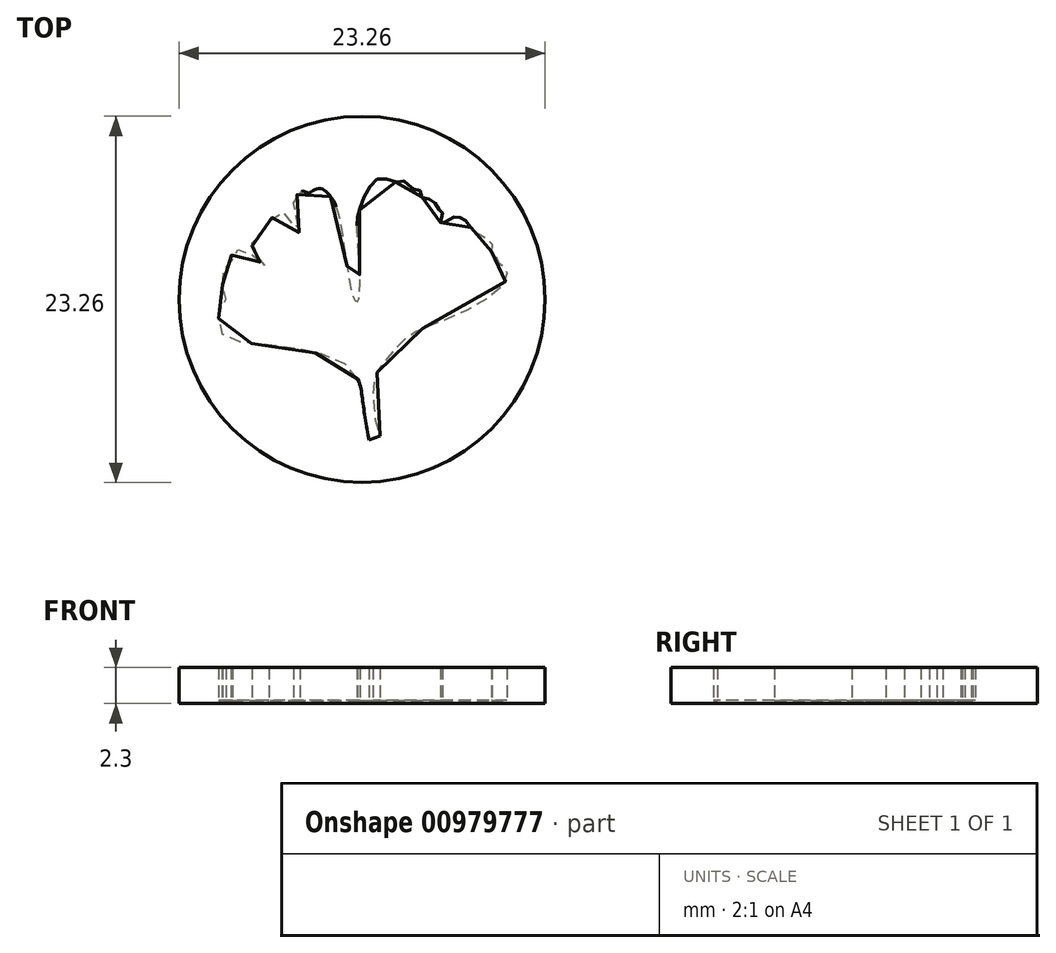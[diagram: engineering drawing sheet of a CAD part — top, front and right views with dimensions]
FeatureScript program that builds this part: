
annotation { "Feature Type Name" : "Feature", "Feature Type Description" : "" }
export const myFeature = defineFeature(function(context is Context, id is Id, definition is map)
    precondition{}
    {
        {
            var Q0;
            Q0=qCreatedBy(makeId("Top.planeOp"),FACE);
            var sketch = newSketch(context, id + "F0", { "sketchPlane" : qUnion([Q0]), "disableImprinting" : false});
            skCircle(sketch, "E0", {"center": v(0, 0) * mm, "radius": 11.62 * mm});
            skFitSpline(sketch, "E1", {"points": [v(-0.27, -5.05) * mm, v(-0.7, -4.43) * mm, v(-1.87, -3.68) * mm, v(-3.17, -3.35) * mm, v(-4.61, -3.03) * mm, v(-6.9, -2.83) * mm, v(-8.15, -2.6) * mm, v(-8.85, -2.26) * mm, v(-9.1, -1.33) * mm, v(-8.98, -0.31) * mm, v(-8.63, 0) * mm, v(-8.88, 0.58) * mm, v(-8.85, 0.93) * mm, v(-8.88, 1.28) * mm, v(-8.75, 1.88) * mm, v(-8.25, 2.08) * mm, v(-8.3, 2.7) * mm, v(-8.18, 3) * mm, v(-7.73, 3.18) * mm, v(-7.18, 3.03) * mm, v(-6.63, 2.5) * mm, v(-6.2, 2.16) * mm, v(-5.9, 2) * mm, v(-6.7, 2.73) * mm, v(-6.98, 3.3) * mm, v(-6.9, 3.93) * mm, v(-6.46, 4.22) * mm, v(-5.96, 4.6) * mm, v(-5.7, 5.15) * mm, v(-5.39, 5.62) * mm, v(-4.74, 5.32) * mm, v(-4.39, 4.75) * mm, v(-3.94, 4.22) * mm, v(-4.24, 5.2) * mm, v(-4.34, 6.14) * mm, v(-4.19, 6.57) * mm, v(-3.79, 6.87) * mm, v(-3.4, 6.77) * mm, v(-2.77, 7.04) * mm, v(-2.02, 6.57) * mm, v(-1.52, 5.47) * mm, v(-1.04, 2.69) * mm, v(-0.48, 0) * mm, v(-0.27, -0.13) * mm, v(-0.2, 2.7) * mm, v(-0.32, 4.7) * mm, v(-0.2, 5.52) * mm, v(0.35, 6.94) * mm, v(1.2, 7.69) * mm, v(2.32, 7.44) * mm, v(2.77, 7.52) * mm, v(3.1, 7.07) * mm, v(3.66, 6.92) * mm, v(3.84, 6.44) * mm, v(4.49, 6.3) * mm, v(4.86, 5.75) * mm, v(5.11, 5.55) * mm, v(5.01, 4.8) * mm, v(5.78, 5.22) * mm, v(6.23, 5.2) * mm, v(6.63, 4.95) * mm, v(7.03, 4.4) * mm, v(7.3, 4.22) * mm, v(7.78, 3.93) * mm, v(8.25, 3.58) * mm, v(8.23, 2.95) * mm, v(8.55, 2.68) * mm, v(8.7, 2.28) * mm, v(8.95, 2.13) * mm, v(9.15, 1.2) * mm, v(5.28, -1.3) * mm, v(3.2, -2.18) * mm, v(1.86, -3.42) * mm, v(0.81, -5.03) * mm, v(0.74, -6.69) * mm, v(1.13, -8.67) * mm], "startDerivative": vector(-26.54, 49.86) * mm, "endDerivative": vector(49.67, -138.43) * mm});
            skFitSpline(sketch, "E2", {"points": [v(-0.27, -5.05) * mm, v(0, -6.16) * mm, v(0.2, -7.5) * mm, v(0.44, -8.93) * mm], "startDerivative": vector(1.9, -3.96) * mm, "endDerivative": vector(0.78, -3.61) * mm});
            skLineSegment(sketch, "E3", {"start": v(0.44, -8.93) * mm, "end": v(1.13, -8.67) * mm});
            skSolve(sketch);
        }
        {
            var Q0;
            Q0 = qSketchRegion(id + "F0", true);
            extrude(context, id + "F1", {"entities" : qUnion([Q0]), "flatOperationType" : FlatOperationType.REMOVE, "depth" : 2.3 * mm, "offsetDistance" : 25 * mm, "domain" : OperationDomain.MODEL});
        }
        {
            var Q0;
            Q0=makeQuery(id+"F0.imprint","IMPRINT",FACE,{"disambiguationData":[TD([[makeQuery(id+"F0.imprint","IMPRINT",EDGE,{"derivedFrom":sQuery(id+"F0.wireOp",EDGE,"E1")}),-1.0]])]});
            extrude(context, id + "F2", {"entities" : qUnion([Q0]), "operationType" : NewBodyOperationType.ADD, "flatOperationType" : FlatOperationType.REMOVE, "depth" : 0.2 * mm, "offsetDistance" : 25 * mm, "domain" : OperationDomain.MODEL});
        }
    });
